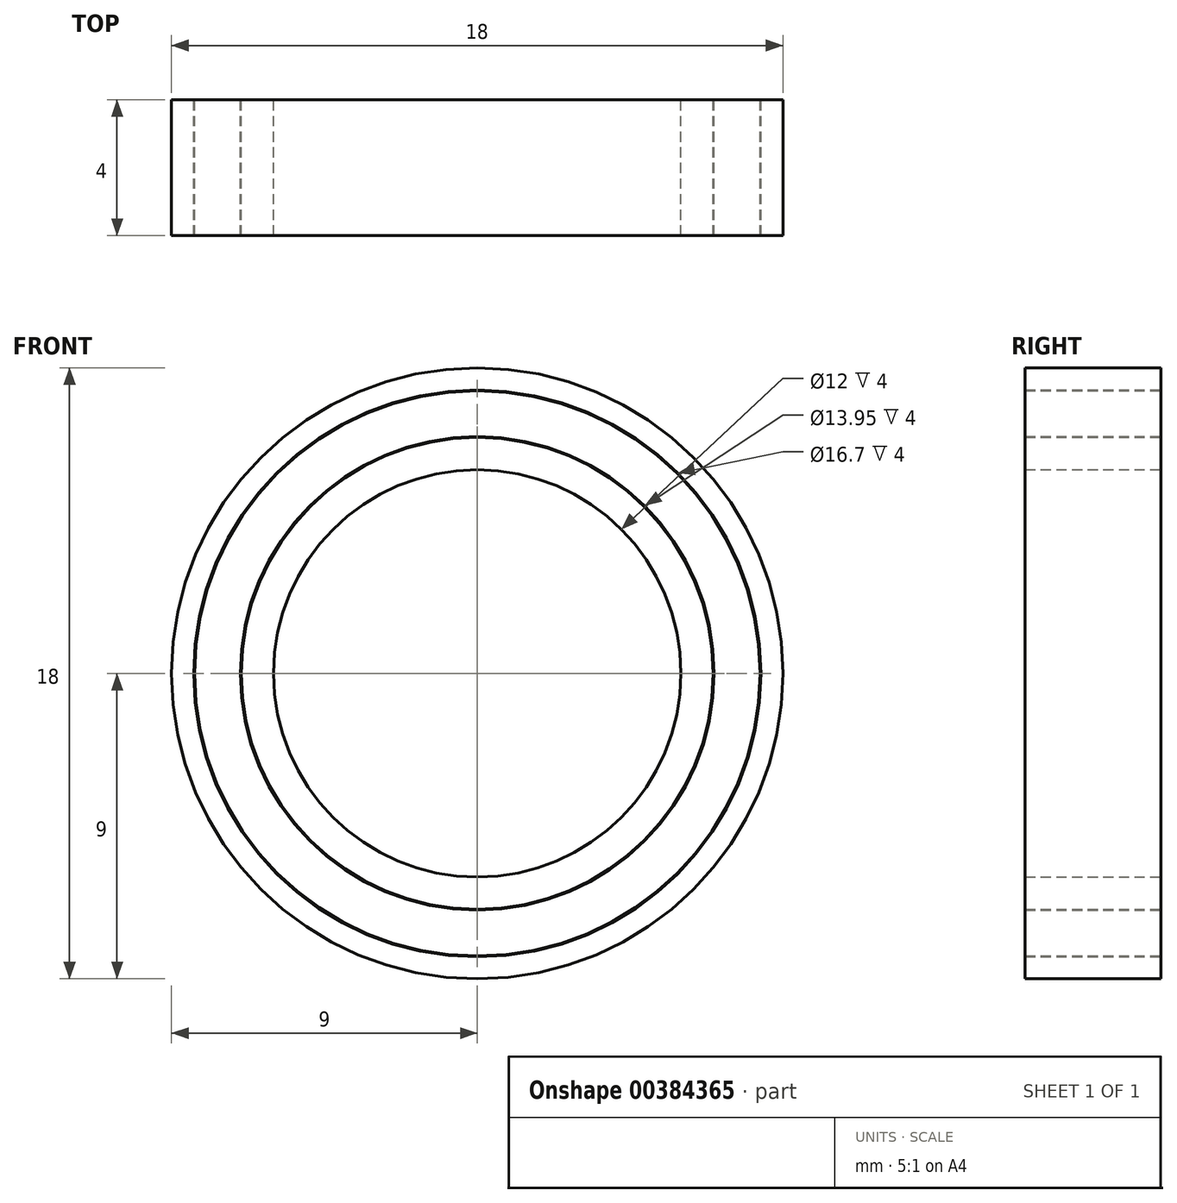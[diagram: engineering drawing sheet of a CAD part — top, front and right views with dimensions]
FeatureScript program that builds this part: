
annotation { "Feature Type Name" : "Feature", "Feature Type Description" : "" }
export const myFeature = defineFeature(function(context is Context, id is Id, definition is map)
    precondition{}
    {
        {
            var Q0;
            Q0=qCreatedBy(makeId("Front.planeOp"),FACE);
            var sketch = newSketch(context, id + "F0", { "sketchPlane" : qUnion([Q0])});
            skCircle(sketch, "E0", {"center": v(0, 0) * mm, "radius": 9 * mm});
            skCircle(sketch, "E1", {"center": v(0, 0) * mm, "radius": 8.35 * mm});
            skCircle(sketch, "E2", {"center": v(0, 0) * mm, "radius": 6.95 * mm});
            skCircle(sketch, "E3", {"center": v(0, 0) * mm, "radius": 6 * mm});
            skSolve(sketch);
        }
        {
            var Q0;
            Q0=makeQuery(id+"F0.imprint","IMPRINT",FACE,{"disambiguationData":[TD([[makeQuery(id+"F0.imprint","IMPRINT",EDGE,{"derivedFrom":sQuery(id+"F0.wireOp",EDGE,"E0")}),1.0]])]});
            extrude(context, id + "F1", {"entities" : qUnion([Q0]), "endBound" : BoundingType.SYMMETRIC, "depth" : 4 * mm, "offsetDistance" : 25.4 * mm});
        }
        {
            var Q0;
            Q0=makeQuery(id+"F0.imprint","IMPRINT",FACE,{"disambiguationData":[TD([[makeQuery(id+"F0.imprint","IMPRINT",EDGE,{"derivedFrom":sQuery(id+"F0.wireOp",EDGE,"E2")}),1.0]])]});
            extrude(context, id + "F2", {"entities" : qUnion([Q0]), "endBound" : BoundingType.SYMMETRIC, "depth" : 4 * mm, "offsetDistance" : 25.4 * mm});
        }
        {
            var Q0;
            Q0=qCreatedBy(makeId("Front.planeOp"),FACE);
            var sketch = newSketch(context, id + "F3", { "sketchPlane" : qUnion([Q0])});
            skCircle(sketch, "E4.0", {"center": v(0, 0) * mm, "radius": 8.32 * mm});
            skCircle(sketch, "E5.0", {"center": v(0, 0) * mm, "radius": 6.98 * mm});
            skSolve(sketch);
        }
        {
            var Q0;
            Q0 = qSketchRegion(id + "F3", true);
            extrude(context, id + "F4", {"entities" : qUnion([Q0]), "endBound" : BoundingType.SYMMETRIC, "depth" : 4 * mm, "offsetDistance" : 25.4 * mm});
        }
    });
